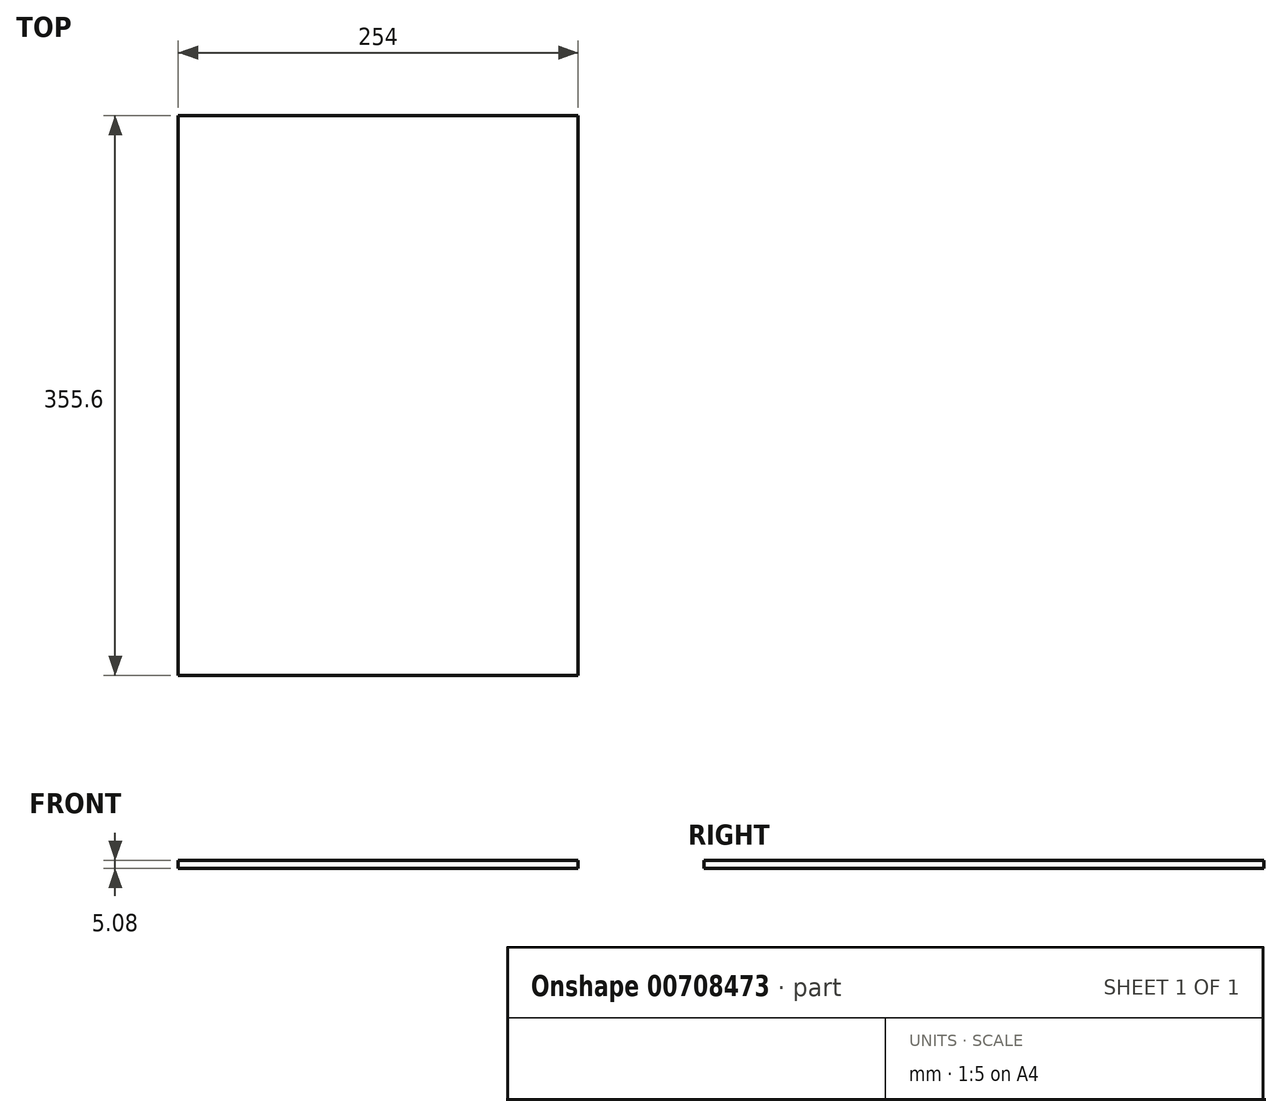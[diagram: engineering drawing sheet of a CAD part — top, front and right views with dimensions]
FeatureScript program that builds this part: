
annotation { "Feature Type Name" : "Feature", "Feature Type Description" : "" }
export const myFeature = defineFeature(function(context is Context, id is Id, definition is map)
    precondition{}
    {
        {
            var Q0;
            Q0=qCreatedBy(makeId("Front.planeOp"),FACE);
            var sketch = newSketch(context, id + "F0", { "sketchPlane" : qUnion([Q0])});
            skLineSegment(sketch, "E0.bottom", {"start": v(-127, -2.54) * mm, "end": v(127, -2.54) * mm});
            skLineSegment(sketch, "E0.top", {"start": v(-127, 2.54) * mm, "end": v(127, 2.54) * mm});
            skLineSegment(sketch, "E0.left", {"start": v(-127, -2.54) * mm, "end": v(-127, 2.54) * mm});
            skLineSegment(sketch, "E0.right", {"start": v(127, -2.54) * mm, "end": v(127, 2.54) * mm});
            skPoint(sketch, "E0.middle", {"position": v(0, 0) * mm});
            skSolve(sketch);
        }
        {
            var Q0;
            Q0 = qSketchRegion(id + "F0", true);
            extrude(context, id + "F1", {"entities" : qUnion([Q0]), "depth" : 355.6 * mm, "offsetDistance" : 25.4 * mm});
        }
    });
